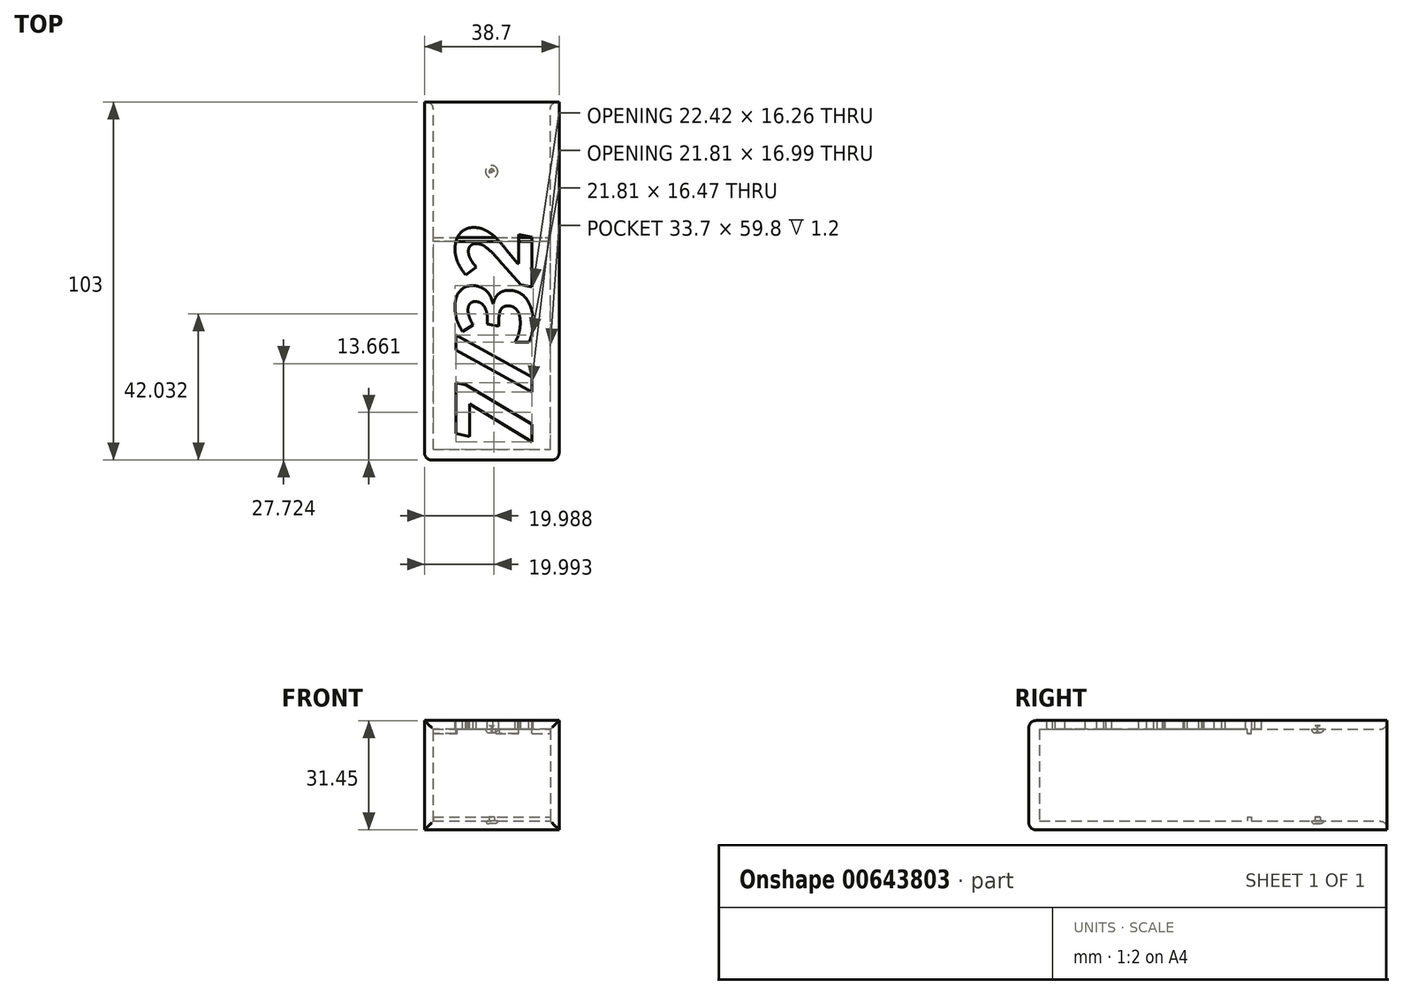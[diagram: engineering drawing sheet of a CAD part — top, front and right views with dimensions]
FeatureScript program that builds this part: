
annotation { "Feature Type Name" : "Feature", "Feature Type Description" : "" }
export const myFeature = defineFeature(function(context is Context, id is Id, definition is map)
    precondition{}
    {
        {
            var Q0;
            Q0=qCreatedBy(makeId("Front.planeOp"),FACE);
            var sketch = newSketch(context, id + "F0", { "sketchPlane" : qUnion([Q0])});
            skLineSegment(sketch, "E0.top", {"start": v(-32.33, 29) * mm, "end": v(1.37, 29) * mm});
            skLineSegment(sketch, "E0.left", {"start": v(-32.33, 2.54) * mm, "end": v(-32.33, 29) * mm});
            skLineSegment(sketch, "E1", {"start": v(1.37, 29) * mm, "end": v(1.37, 2.54) * mm});
            skLineSegment(sketch, "E2", {"start": v(-32.33, 2.54) * mm, "end": v(1.37, 2.54) * mm});
            skLineSegment(sketch, "E3.0", {"start": v(-34.83, 31.5) * mm, "end": v(3.87, 31.5) * mm});
            skLineSegment(sketch, "E3.1", {"start": v(-34.83, 0.04) * mm, "end": v(-34.83, 31.5) * mm});
            skLineSegment(sketch, "E3.2", {"start": v(-34.83, 0.04) * mm, "end": v(3.87, 0.04) * mm});
            skLineSegment(sketch, "E3.3", {"start": v(3.87, 31.5) * mm, "end": v(3.87, 0.04) * mm});
            skSolve(sketch);
        }
        {
            var Q0;
            Q0 = qSketchRegion(id + "F0", true);
            extrude(context, id + "F1", {"entities" : qUnion([Q0]), "depth" : 100 * mm, "offsetDistance" : 25 * mm});
        }
        {
            var Q0;
            Q0=makeQuery(id+"F1.opExtrude","CAP_FACE",FACE,{"disambiguationData":[OSD([sQuery(id+"F0.wireOp",EDGE,"E0.top"),sQuery(id+"F0.wireOp",EDGE,"E0.left"),sQuery(id+"F0.wireOp",EDGE,"E1"),sQuery(id+"F0.wireOp",EDGE,"E2"),sQuery(id+"F0.wireOp",EDGE,"E3.0"),sQuery(id+"F0.wireOp",EDGE,"E3.1"),sQuery(id+"F0.wireOp",EDGE,"E3.2"),sQuery(id+"F0.wireOp",EDGE,"E3.3")])],"isStart":false});
            var sketch = newSketch(context, id + "F2", { "sketchPlane" : qUnion([Q0])});
            skLineSegment(sketch, "E4.bottom", {"start": v(-34.83, 31.5) * mm, "end": v(3.87, 31.5) * mm});
            skLineSegment(sketch, "E4.top", {"start": v(-34.83, 0.04) * mm, "end": v(3.87, 0.04) * mm});
            skLineSegment(sketch, "E4.left", {"start": v(-34.83, 31.5) * mm, "end": v(-34.83, 0.04) * mm});
            skLineSegment(sketch, "E4.right", {"start": v(3.87, 31.5) * mm, "end": v(3.87, 0.04) * mm});
            skSolve(sketch);
        }
        {
            var Q0;
            Q0 = qSketchRegion(id + "F2", true);
            extrude(context, id + "F3", {"entities" : qUnion([Q0]), "operationType" : NewBodyOperationType.ADD, "depth" : 3 * mm, "offsetDistance" : 25 * mm});
        }
        {
            var Q0;
            Q0=makeQuery(id+"F1.opExtrude","CAP_EDGE",EDGE,{"disambiguationData":[OSD([sQuery(id+"F0.wireOp",EDGE,"E2")])],"isStart":true});
            var Q1;
            Q1=makeQuery(id+"F1.opExtrude","CAP_EDGE",EDGE,{"disambiguationData":[OSD([sQuery(id+"F0.wireOp",EDGE,"E1")])],"isStart":true});
            var Q2;
            Q2=makeQuery(id+"F1.opExtrude","CAP_EDGE",EDGE,{"disambiguationData":[OSD([sQuery(id+"F0.wireOp",EDGE,"E0.top")])],"isStart":true});
            var Q3;
            Q3=makeQuery(id+"F1.opExtrude","CAP_EDGE",EDGE,{"disambiguationData":[OSD([sQuery(id+"F0.wireOp",EDGE,"E0.left")])],"isStart":true});
            var Q4;
            Q4=makeQuery(id+"F3.opExtrude","CAP_EDGE",EDGE,{"disambiguationData":[OSD([sQuery(id+"F2.wireOp",EDGE,"E4.bottom")])],"isStart":false});
            var Q5;
            Q5=makeQuery(id+"F3.opExtrude","CAP_EDGE",EDGE,{"disambiguationData":[OSD([sQuery(id+"F2.wireOp",EDGE,"E4.right")])],"isStart":false});
            var Q6;
            Q6=makeQuery(id+"F3.opExtrude","CAP_EDGE",EDGE,{"disambiguationData":[OSD([sQuery(id+"F2.wireOp",EDGE,"E4.top")])],"isStart":false});
            var Q7;
            Q7=makeQuery(id+"F3.opExtrude","CAP_EDGE",EDGE,{"disambiguationData":[OSD([sQuery(id+"F2.wireOp",EDGE,"E4.left")])],"isStart":false});
            fillet(context, id + "F4", {"entities" : qUnion([Q0, Q1, Q2, Q3, Q4, Q5, Q6, Q7]), "radius" : 2 * mm, "tangentPropagation" : true, "allowEdgeOverflow" : false});
        }
        {
            var Q0;
            Q0=makeQuery(id+"F3.boolean.opBoolean","MERGE",FACE,{"derivedFrom":[makeQuery(id+"F1.opExtrude","SWEPT_FACE",FACE,{"disambiguationData":[OSD([sQuery(id+"F0.wireOp",EDGE,"E3.0")])]}),makeQuery(id+"F3.opExtrude","SWEPT_FACE",FACE,{"disambiguationData":[OSD([sQuery(id+"F2.wireOp",EDGE,"E4.bottom")])]})]});
            var sketch = newSketch(context, id + "F5", { "sketchPlane" : qUnion([Q0])});
            skText(sketch, "E5", { "text": "7/32", "fontName": "OpenSans-BoldItalic.ttf"});
            const initialGuessF5  = {"E5": [-0.00393, -0.099, 0, 1, 0.022]};
            skSetInitialGuess(sketch, initialGuessF5);
            skSolve(sketch);
        }
        {
            var Q0;
            Q0 = qSketchRegion(id + "F5", true);
            extrude(context, id + "F6", {"entities" : qUnion([Q0]), "operationType" : NewBodyOperationType.REMOVE, "oppositeDirection" : true, "depth" : 2.7 * mm, "offsetDistance" : 25 * mm});
        }
        {
            var Q0;
            Q0=makeQuery(id+"F1.opExtrude","SWEPT_FACE",FACE,{"disambiguationData":[OSD([sQuery(id+"F0.wireOp",EDGE,"E2")])]});
            var sketch = newSketch(context, id + "F7", { "sketchPlane" : qUnion([Q0])});
            skPoint(sketch, "E6.0", {"position": v(-15.48, 0) * mm});
            skLineSegment(sketch, "E7", {"start": v(-15.53, -4.6) * mm, "end": v(-15.48, -72.77) * mm, "construction": true});
            skLineSegment(sketch, "E8.0", {"start": v(-34.33, 0) * mm, "end": v(3.37, 0) * mm});
            skCircle(sketch, "E9", {"center": v(-15.52, -20) * mm, "radius": 1.75 * mm});
            skSolve(sketch);
        }
        {
            var Q0;
            Q0 = qSketchRegion(id + "F7", true);
            extrude(context, id + "F8", {"entities" : qUnion([Q0]), "operationType" : NewBodyOperationType.REMOVE, "oppositeDirection" : true, "depth" : .75 * mm, "offsetDistance" : 25 * mm});
        }
        {
            var Q0;
            Q0=makeQuery(id+"F8.boolean.opBoolean","COPY",EDGE,{"derivedFrom":makeQuery(id+"F8.opExtrude","CAP_EDGE",EDGE,{"disambiguationData":[OSD([sQuery(id+"F7.wireOp",EDGE,"E9")])],"isStart":false})});
            fillet(context, id + "F9", {"entities" : qUnion([Q0]), "radius" : 1 * mm, "tangentPropagation" : true, "allowEdgeOverflow" : false});
        }
        {
            var Q0;
            Q0=makeQuery(id+"F1.opExtrude","SWEPT_FACE",FACE,{"disambiguationData":[OSD([sQuery(id+"F0.wireOp",EDGE,"E0.top")])]});
            var sketch = newSketch(context, id + "F10", { "sketchPlane" : qUnion([Q0])});
            skCircle(sketch, "E10.0", {"center": v(-15.52, 20) * mm, "radius": 1.75 * mm});
            skSolve(sketch);
        }
        {
            var Q0;
            Q0 = qSketchRegion(id + "F10", true);
            extrude(context, id + "F11", {"entities" : qUnion([Q0]), "operationType" : NewBodyOperationType.REMOVE, "oppositeDirection" : true, "depth" : 1 * mm, "offsetDistance" : 25 * mm});
        }
        {
            var Q0;
            Q0=makeQuery(id+"F11.boolean.opBoolean","COPY",EDGE,{"derivedFrom":makeQuery(id+"F11.opExtrude","CAP_EDGE",EDGE,{"disambiguationData":[OSD([sQuery(id+"F10.wireOp",EDGE,"E10.0")])],"isStart":false})});
            fillet(context, id + "F12", {"entities" : qUnion([Q0]), "radius" : 1 * mm, "tangentPropagation" : true, "allowEdgeOverflow" : false});
        }
        {
            var Q0;
            Q0=makeQuery(id+"F1.opExtrude","SWEPT_FACE",FACE,{"disambiguationData":[OSD([sQuery(id+"F0.wireOp",EDGE,"E2")])]});
            var sketch = newSketch(context, id + "F13", { "sketchPlane" : qUnion([Q0])});
            skLineSegment(sketch, "E11", {"start": v(-32.33, -39) * mm, "end": v(1.37, -39) * mm});
            skLineSegment(sketch, "E12", {"start": v(1.37, -39) * mm, "end": v(1.37, -40.2) * mm});
            skLineSegment(sketch, "E13", {"start": v(1.37, -40.2) * mm, "end": v(-32.33, -40.2) * mm});
            skLineSegment(sketch, "E14", {"start": v(-32.33, -40.2) * mm, "end": v(-32.33, -39) * mm});
            skCircle(sketch, "E15.0", {"center": v(-15.52, -20) * mm, "radius": 0.75 * mm});
            skSolve(sketch);
        }
        {
            var Q0;
            Q0 = qSketchRegion(id + "F13", true);
            extrude(context, id + "F14", {"entities" : qUnion([Q0]), "operationType" : NewBodyOperationType.ADD, "depth" : 1.2 * mm, "offsetDistance" : 25 * mm});
        }
        {
            var Q0;
            Q0=makeQuery(id+"F1.opExtrude","SWEPT_FACE",FACE,{"disambiguationData":[OSD([sQuery(id+"F0.wireOp",EDGE,"E0.top")])]});
            var sketch = newSketch(context, id + "F15", { "sketchPlane" : qUnion([Q0])});
            skLineSegment(sketch, "E16.0", {"start": v(-32.33, 39) * mm, "end": v(1.37, 39) * mm});
            skLineSegment(sketch, "E17.0", {"start": v(1.37, 40.2) * mm, "end": v(-32.33, 40.2) * mm});
            skSolve(sketch);
        }
        {
            var Q0;
            {var subQ0=sQuery(id+"F15.wireOp",EDGE,"E16.0");var subQ1=sQuery(id+"F0.wireOp",EDGE,"E0.top");var subQ2=makeQuery(id+"F1.opExtrude","SWEPT_EDGE",EDGE,{"disambiguationData":[OSD([subQ1,sQuery(id+"F0.wireOp",EDGE,"E0.left")])]});var subQ3=makeQuery(id+"F15.imprint","INTERSECT",VERTEX,{"derivedFrom":[subQ2,subQ0]});Q0=makeQuery(id+"F15.imprint","IMPRINT",FACE,{"disambiguationData":[TD([[makeQuery(id+"F15.imprint","IMPRINT",EDGE,{"disambiguationData":[TD([[subQ3,-1.0]])],"derivedFrom":subQ0}),1.0]])]});}
            var Q1;
            {var subQ0=sQuery(id+"F15.wireOp",EDGE,"E16.0");var subQ1=sQuery(id+"F0.wireOp",EDGE,"E0.top");var subQ2=makeQuery(id+"F1.opExtrude","SWEPT_EDGE",EDGE,{"disambiguationData":[OSD([subQ1,sQuery(id+"F0.wireOp",EDGE,"E1")])]});var subQ3=makeQuery(id+"F15.imprint","INTERSECT",VERTEX,{"derivedFrom":[subQ2,subQ0]});Q1=makeQuery(id+"F15.imprint","IMPRINT",FACE,{"disambiguationData":[TD([[makeQuery(id+"F15.imprint","IMPRINT",EDGE,{"disambiguationData":[TD([[subQ3,1.0]])],"derivedFrom":subQ0}),1.0]])]});}
            var Q2;
            {var subQ0=sQuery(id+"F15.wireOp",EDGE,"E16.0");var subQ1=makeQuery(id+"F1.opExtrude","SWEPT_FACE",FACE,{"disambiguationData":[OSD([sQuery(id+"F0.wireOp",EDGE,"E0.top")])]});var subQ2=makeQuery(id+"F6.boolean.opBoolean","INTERSECT",EDGE,{"derivedFrom":[subQ1,makeQuery(id+"F6.opExtrude","SWEPT_FACE",FACE,{"disambiguationData":[OSD([sQuery(id+"F5.wireOp",EDGE,"E5.sketch_text.stroke-55")])]})]});var subQ3=makeQuery(id+"F15.imprint","INTERSECT",VERTEX,{"derivedFrom":[subQ2,subQ0]});Q2=makeQuery(id+"F15.imprint","IMPRINT",FACE,{"disambiguationData":[TD([[makeQuery(id+"F15.imprint","IMPRINT",EDGE,{"disambiguationData":[TD([[subQ3,-1.0]])],"derivedFrom":subQ0}),1.0]])]});}
            extrude(context, id + "F16", {"entities" : qUnion([Q0, Q1, Q2]), "operationType" : NewBodyOperationType.ADD, "depth" : 1.2 * mm, "offsetDistance" : 25 * mm});
        }
    });
